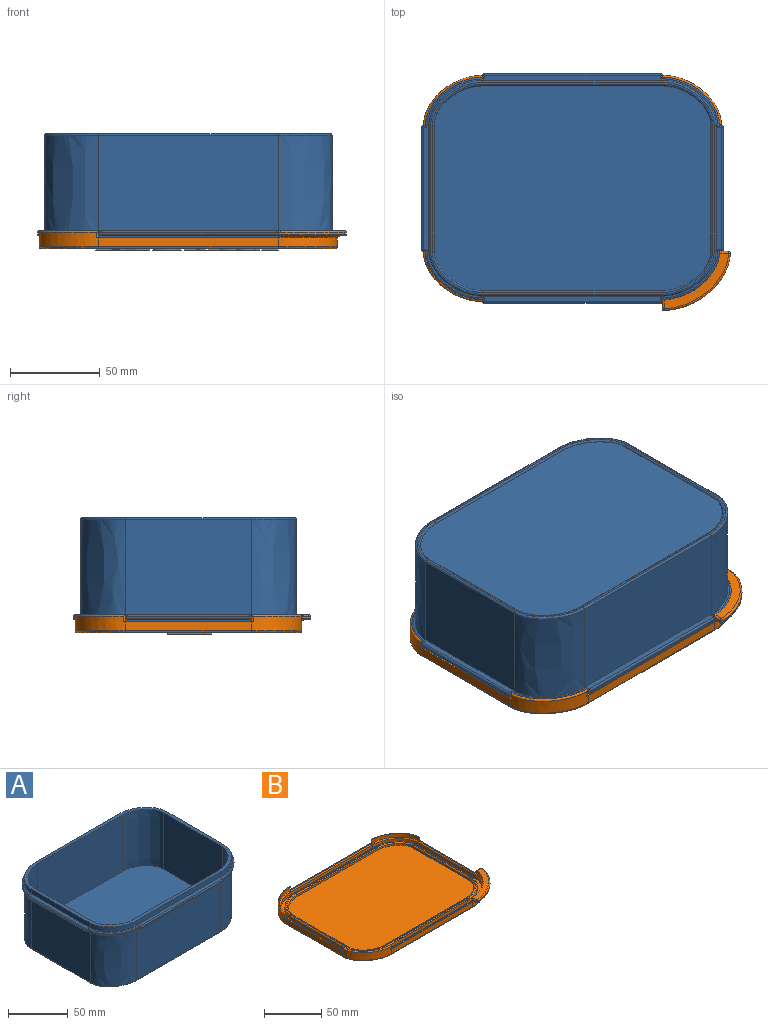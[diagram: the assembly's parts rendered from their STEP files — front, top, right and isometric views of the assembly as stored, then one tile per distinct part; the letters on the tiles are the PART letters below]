
ASSEMBLY  parts=2 mates=1
PART A: 118 faces, bbox 168x128x62 mm
  f0: extruded ~30x25mm, area 213.5mm2, adj f1,f15,f16,f34
  f1: plane 100x5mm, normal (0,-1,0), area 500mm2, adj f0,f2,f16,f34
  f2: extruded ~30x25mm, area 213.5mm2, adj f1,f3,f16,f34
  f3: plane 70x5mm, normal (1,0,0), area 350mm2, adj f2,f4,f16,f34
  f4: extruded ~30x25mm, area 213.5mm2, adj f3,f5,f16,f34
  f5: plane 100x5mm, normal (0,1,0), area 500mm2, adj f4,f6,f16,f34
  f6: extruded ~30x25mm, area 213.5mm2, adj f5,f15,f16,f34
  f7: extruded ~58x27mm, area 2202.8mm2, adj f8,f14,f16,f117
  f8: plane 100x58mm, normal (0,1,0), area 5800mm2, adj f7,f9,f16,f117
  f9: extruded ~58x27mm, area 2202.8mm2, adj f8,f10,f16,f117
  f10: plane 70x58mm, normal (1,0,0), area 4060mm2, adj f9,f11,f16,f117
  f11: extruded ~58x27mm, area 2202.8mm2, adj f10,f12,f16,f117
  f12: plane 100x58mm, normal (0,-1,0), area 5800mm2, adj f11,f13,f16,f117
  f13: extruded ~58x27mm, area 2202.8mm2, adj f12,f14,f16,f117
  f14: plane 70x58mm, normal (-1,0,0), area 4060mm2, adj f7,f13,f16,f117
  f15: plane 70x5mm, normal (-1,0,0), area 350mm2, adj f0,f6,f16,f34
  f16: plane 160x120mm, normal (0,0,1), area 1504mm2, adj f0,f1,f2,f3,f4,f5,f6,f7
  f17: plane 166x126mm, normal (0,0,-1), area 1177.9mm2, adj f67,f68,f70,f71,f74,f75,f77,f78
  f18: plane 1x1mm, normal (0,1,0), area 1mm2, adj f33,f47,f51,f75
  f19: plane 68x1mm, normal (-1,0,0), area 68mm2, adj f45,f51,f53,f71
  f20: plane 1x1mm, normal (0,-1,0), area 1mm2, adj f21,f43,f53,f67
  f21: extruded ~32x27mm, area 45.8mm2, adj f20,f22,f41,f68
  f22: plane 1x1mm, normal (-1,0,0), area 1mm2, adj f21,f39,f55,f70
  f23: plane 98x1mm, normal (0,-1,0), area 98mm2, adj f37,f55,f57,f74
  f24: plane 1x1mm, normal (1,0,0), area 1mm2, adj f25,f35,f57,f78
  f25: extruded ~32x27mm, area 45.8mm2, adj f24,f26,f36,f80
  f26: plane 1x1mm, normal (0,-1,0), area 1mm2, adj f25,f38,f59,f82
  f27: plane 68x1mm, normal (1,0,0), area 68mm2, adj f40,f59,f61,f86
  f28: plane 1x1mm, normal (0,1,0), area 1mm2, adj f29,f42,f61,f90
  f29: extruded ~32x27mm, area 45.8mm2, adj f28,f30,f44,f89
  f30: plane 1x1mm, normal (1,0,0), area 1mm2, adj f29,f46,f63,f87
  f31: plane 98x1mm, normal (0,1,0), area 98mm2, adj f48,f63,f65,f83
  f32: plane 1x1mm, normal (-1,0,0), area 1mm2, adj f33,f50,f65,f79
  f33: extruded ~32x27mm, area 45.8mm2, adj f18,f32,f49,f77
  f34: plane 166x126mm, normal (0,0,1), area 1177.9mm2, adj f0,f1,f2,f3,f4,f5,f6,f15
  f35: cylinder r=1mm len=2mm, axis (0,-1,0), area 2.4mm2, adj f24,f34,f36,f58
  f36: bspline ~33.32x31.21mm, area 72.7mm2, adj f25,f34,f35,f38
  f37: cylinder r=1mm len=98mm, axis (-1,0,0), area 153.9mm2, adj f23,f34,f56,f58
  f38: cylinder r=1mm len=2mm, axis (-1,0,0), area 2.4mm2, adj f26,f34,f36,f60
  f39: cylinder r=1mm len=2mm, axis (0,1,0), area 2.4mm2, adj f22,f34,f41,f56
  f40: cylinder r=1mm len=68mm, axis (0,-1,0), area 106.8mm2, adj f27,f34,f60,f62
  f41: bspline ~33.32x31.21mm, area 72.7mm2, adj f21,f34,f39,f43
  f42: cylinder r=1mm len=2mm, axis (1,0,0), area 2.4mm2, adj f28,f34,f44,f62
  f43: cylinder r=1mm len=2mm, axis (-1,0,0), area 2.4mm2, adj f20,f34,f41,f54
  f44: bspline ~33.32x31.21mm, area 72.7mm2, adj f29,f34,f42,f46
  f45: cylinder r=1mm len=68mm, axis (0,1,0), area 106.8mm2, adj f19,f34,f52,f54
  f46: cylinder r=1mm len=2mm, axis (0,-1,0), area 2.4mm2, adj f30,f34,f44,f64
  f47: cylinder r=1mm len=2mm, axis (1,0,0), area 2.4mm2, adj f18,f34,f49,f52
  f48: cylinder r=1mm len=98mm, axis (1,0,0), area 153.9mm2, adj f31,f34,f64,f66
  f49: bspline ~33.32x31.21mm, area 72.7mm2, adj f33,f34,f47,f50
  f50: cylinder r=1mm len=2mm, axis (0,1,0), area 2.4mm2, adj f32,f34,f49,f66
  f51: cylinder r=1mm len=1mm, axis (0,0,1), area 1.6mm2, adj f18,f19,f52,f73
  f52: sphere r=1mm, area 2.1mm2, adj f45,f47,f51
  f53: cylinder r=1mm len=1mm, axis (0,0,-1), area 1.6mm2, adj f19,f20,f54,f69
  f54: sphere r=1mm, area 1.6mm2, adj f43,f45,f53
  f55: cylinder r=1mm len=1mm, axis (0,0,-1), area 1.6mm2, adj f22,f23,f56,f72
  f56: sphere r=1mm, area 1.6mm2, adj f37,f39,f55
  f57: cylinder r=1mm len=1mm, axis (0,0,1), area 1.6mm2, adj f23,f24,f58,f76
  f58: sphere r=1mm, area 1.6mm2, adj f35,f37,f57
  f59: cylinder r=1mm len=1mm, axis (0,0,-1), area 1.6mm2, adj f26,f27,f60,f84
  f60: sphere r=1mm, area 1.6mm2, adj f38,f40,f59
  f61: cylinder r=1mm len=1mm, axis (0,0,1), area 1.6mm2, adj f27,f28,f62,f88
  f62: sphere r=1mm, area 1mm2, adj f40,f42,f61
  f63: cylinder r=1mm len=1mm, axis (0,0,1), area 1.6mm2, adj f30,f31,f64,f85
  f64: sphere r=1mm, area 1mm2, adj f46,f48,f63
  f65: cylinder r=1mm len=1mm, axis (0,0,-1), area 1.6mm2, adj f31,f32,f66,f81
  f66: sphere r=1mm, area 2.1mm2, adj f48,f50,f65
  f67: cylinder r=1mm len=2mm, axis (1,0,0), area 2.4mm2, adj f17,f20,f68,f69
  f68: bspline ~33.32x31.21mm, area 72.7mm2, adj f17,f21,f67,f70
  f69: sphere r=1mm, area 1.6mm2, adj f53,f67,f71
  f70: cylinder r=1mm len=2mm, axis (0,-1,0), area 2.4mm2, adj f17,f22,f68,f72
  f71: cylinder r=1mm len=68mm, axis (0,-1,0), area 106.8mm2, adj f17,f19,f69,f73
  f72: sphere r=1mm, area 1.6mm2, adj f55,f70,f74
  f73: sphere r=1mm, area 2.1mm2, adj f51,f71,f75
  f74: cylinder r=1mm len=98mm, axis (1,0,0), area 153.9mm2, adj f17,f23,f72,f76
  f75: cylinder r=1mm len=2mm, axis (-1,0,0), area 2.4mm2, adj f17,f18,f73,f77
  f76: sphere r=1mm, area 1.6mm2, adj f57,f74,f78
  f77: bspline ~33.32x31.21mm, area 72.7mm2, adj f17,f33,f75,f79
  f78: cylinder r=1mm len=2mm, axis (0,1,0), area 2.4mm2, adj f17,f24,f76,f80
  f79: cylinder r=1mm len=2mm, axis (0,-1,0), area 2.4mm2, adj f17,f32,f77,f81
  f80: bspline ~33.32x31.21mm, area 72.7mm2, adj f17,f25,f78,f82
  f81: sphere r=1mm, area 2.1mm2, adj f65,f79,f83
  f82: cylinder r=1mm len=2mm, axis (1,0,0), area 2.4mm2, adj f17,f26,f80,f84
  f83: cylinder r=1mm len=98mm, axis (-1,0,0), area 153.9mm2, adj f17,f31,f81,f85
  f84: sphere r=1mm, area 1.6mm2, adj f59,f82,f86
  f85: sphere r=1mm, area 1mm2, adj f63,f83,f87
  f86: cylinder r=1mm len=68mm, axis (0,1,0), area 106.8mm2, adj f17,f27,f84,f88
  f87: cylinder r=1mm len=2mm, axis (0,1,0), area 2.4mm2, adj f17,f30,f85,f89
  f88: sphere r=1mm, area 1mm2, adj f61,f86,f90
  f89: bspline ~33.32x31.21mm, area 72.7mm2, adj f17,f29,f87,f90
  f90: cylinder r=1mm len=2mm, axis (-1,0,0), area 2.4mm2, adj f17,f28,f88,f89
  f91: bspline ~40.83x27.8mm, area 66.2mm2, adj f92,f93,f107,f115
  f92: cylinder r=1mm len=70mm, axis (0,-1,0), area 110mm2, adj f91,f94,f107,f108
  f93: cylinder r=1mm len=100mm, axis (1,0,0), area 157.1mm2, adj f91,f95,f107,f114
  f94: bspline ~40.83x35.83mm, area 66.2mm2, adj f92,f96,f107,f109
  f95: bspline ~40.83x35.83mm, area 66.2mm2, adj f93,f97,f107,f113
  f96: cylinder r=1mm len=100mm, axis (-1,0,0), area 157.1mm2, adj f94,f98,f107,f110
  f97: cylinder r=1mm len=70mm, axis (0,1,0), area 110mm2, adj f95,f98,f107,f112
  f98: bspline ~35.83x32.76mm, area 66.2mm2, adj f96,f97,f107,f111
  f99: cylinder r=1mm len=70mm, axis (0,-1,0), area 110mm2, adj f100,f101,f107,f116
  f100: bspline ~36.6x31.6mm, area 60.6mm2, adj f99,f102,f107,f116
  f101: bspline ~36.6x31.6mm, area 60.6mm2, adj f99,f103,f107,f116
  f102: cylinder r=1mm len=100mm, axis (-1,0,0), area 157.1mm2, adj f100,f104,f107,f116
  f103: cylinder r=1mm len=100mm, axis (1,0,0), area 157.1mm2, adj f101,f105,f107,f116
  f104: bspline ~36.6x31.6mm, area 60.6mm2, adj f102,f106,f107,f116
  f105: bspline ~36.6x31.6mm, area 60.6mm2, adj f103,f106,f107,f116
  f106: cylinder r=1mm len=70mm, axis (0,1,0), area 110mm2, adj f104,f105,f107,f116
  f107: plane 158x118mm, normal (0,0,-1), area 501.2mm2, adj f91,f92,f93,f94,f95,f96,f97,f98
  f108: plane 70x53mm, normal (-1,0,0), area 3710mm2, adj f17,f92,f109,f115
  f109: extruded ~53x30mm, area 2262.6mm2, adj f17,f94,f108,f110
  f110: plane 100x53mm, normal (0,1,0), area 5300mm2, adj f17,f96,f109,f111
  f111: extruded ~53x30mm, area 2262.6mm2, adj f17,f98,f110,f112
  f112: plane 70x53mm, normal (1,0,0), area 3710mm2, adj f17,f97,f111,f113
  f113: extruded ~53x30mm, area 2262.6mm2, adj f17,f95,f112,f114
  f114: plane 100x53mm, normal (0,-1,0), area 5300mm2, adj f17,f93,f113,f115
  f115: extruded ~53x30mm, area 2262.6mm2, adj f17,f91,f108,f114
  f116: plane 154x114mm, normal (0,0,-1), area 16983.5mm2, adj f99,f100,f101,f102,f103,f104,f105,f106
  f117: plane 154x114mm, normal (0,0,1), area 16983.5mm2, adj f7,f8,f9,f10,f11,f12,f13,f14
PART B: 247 faces, bbox 171.4x131.4x11.4 mm
  f0: extruded ~33x28mm, area 237.2mm2, adj f32,f33,f61,f73,f74,f84,f85,f86
  f1: plane 101.04x1mm, normal (0,0,1), area 100.2mm2, adj f32,f38,f51,f73,f104
  f2: plane 102.07x1mm, normal (0,0,1), area 100.4mm2, adj f34,f35,f36,f50,f100,f101
  f3: plane 71.06x1mm, normal (0,0,1), area 70.2mm2, adj f33,f34,f54,f74,f99
  f4: plane 72.11x1mm, normal (0,0,1), area 70.5mm2, adj f36,f37,f38,f47,f102,f103
  f5: extruded ~24x19mm, area 66.5mm2, adj f6,f20,f63,f70
  f6: plane 100x2mm, normal (0,-1,0), area 200mm2, adj f5,f7,f63,f68
  f7: extruded ~24x19mm, area 66.5mm2, adj f6,f8,f63,f66
  f8: plane 70x2mm, normal (-1,0,0), area 140mm2, adj f7,f9,f63,f64
  f9: extruded ~24x19mm, area 66.5mm2, adj f8,f10,f63,f65
  f10: plane 100x2mm, normal (0,1,0), area 200mm2, adj f9,f11,f63,f67
  f11: extruded ~24x19mm, area 66.5mm2, adj f10,f20,f63,f69
  f12: plane 70x3mm, normal (1,0,0), area 210mm2, adj f13,f19,f23,f46
  f13: extruded ~27x22mm, area 113.9mm2, adj f12,f14,f23,f44
  f14: plane 100x3mm, normal (0,1,0), area 300mm2, adj f13,f15,f23,f42
  f15: extruded ~27x22mm, area 113.9mm2, adj f14,f16,f23,f40
  f16: plane 70x3mm, normal (-1,0,0), area 210mm2, adj f15,f17,f23,f39
  f17: extruded ~27x22mm, area 113.9mm2, adj f16,f18,f23,f41
  f18: plane 100x3mm, normal (0,-1,0), area 300mm2, adj f17,f19,f23,f43
  f19: extruded ~27x22mm, area 113.9mm2, adj f12,f18,f23,f45
  f20: plane 70x2mm, normal (1,0,0), area 140mm2, adj f5,f11,f63,f71
  f21: plane 152x112mm, normal (0,0,1), area 482.4mm2, adj f39,f40,f41,f42,f43,f44,f45,f46
  f22: plane 164x124mm, normal (0,0,-1), area 18436.6mm2, adj f55,f56,f57,f58,f59,f60,f61,f62
  f23: plane 162x122mm, normal (0,0,1), area 2017.5mm2, adj f12,f13,f14,f15,f16,f17,f18,f19
  f24: plane 100x3mm, normal (0,1,0), area 300mm2, adj f23,f25,f31,f51
  f25: extruded ~31x26mm, area 132.7mm2, adj f23,f24,f26,f53
  f26: plane 70x3mm, normal (-1,0,0), area 210mm2, adj f23,f25,f27,f54
  f27: extruded ~31x26mm, area 132.7mm2, adj f23,f26,f28,f52
  f28: plane 100x3mm, normal (0,-1,0), area 300mm2, adj f23,f27,f29,f50
  f29: extruded ~31x26mm, area 132.7mm2, adj f23,f28,f30,f48
  f30: plane 70x3mm, normal (1,0,0), area 210mm2, adj f23,f29,f31,f47
  f31: extruded ~31x26mm, area 132.7mm2, adj f23,f24,f30,f49
  f32: plane 100x5mm, normal (0,-1,0), area 500mm2, adj f0,f1,f38,f59
  f33: plane 70x5mm, normal (1,0,0), area 350mm2, adj f0,f3,f34,f62
  f34: extruded ~33x28mm, area 372.8mm2, adj f2,f3,f33,f35,f60,f98,f99,f100
  f35: plane 100x5mm, normal (0,1,0), area 500mm2, adj f2,f34,f36,f58
  f36: extruded ~33x28mm, area 372.8mm2, adj f2,f4,f35,f37,f56,f97,f101,f102
  f37: plane 70x5mm, normal (-1,0,0), area 350mm2, adj f4,f36,f38,f55
  f38: extruded ~33x28mm, area 372.8mm2, adj f1,f4,f32,f37,f57,f96,f103,f104
  f39: cylinder r=1mm len=70mm, axis (0,1,0), area 110mm2, adj f16,f21,f40,f41
  f40: bspline ~35.45x30.45mm, area 58.7mm2, adj f15,f21,f39,f42
  f41: bspline ~35.45x30.45mm, area 58.7mm2, adj f17,f21,f39,f43
  f42: cylinder r=1mm len=100mm, axis (1,0,0), area 157.1mm2, adj f14,f21,f40,f44
  f43: cylinder r=1mm len=100mm, axis (-1,0,0), area 157.1mm2, adj f18,f21,f41,f45
  f44: bspline ~35.45x30.45mm, area 58.7mm2, adj f13,f21,f42,f46
  f45: bspline ~35.45x30.45mm, area 58.7mm2, adj f19,f21,f43,f46
  f46: cylinder r=1mm len=70mm, axis (0,-1,0), area 110mm2, adj f12,f21,f44,f45
  f47: cylinder r=1mm len=70mm, axis (0,-1,0), area 110mm2, adj f4,f30,f48,f49
  f48: bspline ~43.22x38.22mm, area 70.4mm2, adj f29,f47,f50,f77
  f49: bspline ~43.22x38.22mm, area 70.4mm2, adj f31,f47,f51,f78
  f50: cylinder r=1mm len=100mm, axis (-1,0,0), area 157.1mm2, adj f2,f28,f48,f52
  f51: cylinder r=1mm len=100mm, axis (1,0,0), area 157.1mm2, adj f1,f24,f49,f53
  f52: bspline ~43.22x38.22mm, area 70.4mm2, adj f27,f50,f54,f76
  f53: bspline ~43.22x29.81mm, area 70.4mm2, adj f25,f51,f54,f72
  f54: cylinder r=1mm len=70mm, axis (0,1,0), area 110mm2, adj f3,f26,f52,f53
  f55: cylinder r=1mm len=70mm, axis (0,-1,0), area 110mm2, adj f22,f37,f56,f57
  f56: bspline ~45.49x40.49mm, area 73.5mm2, adj f22,f36,f55,f58
  f57: bspline ~45.49x40.49mm, area 73.5mm2, adj f22,f38,f55,f59
  f58: cylinder r=1mm len=100mm, axis (-1,0,0), area 157.1mm2, adj f22,f35,f56,f60
  f59: cylinder r=1mm len=100mm, axis (1,0,0), area 157.1mm2, adj f22,f32,f57,f61
  f60: bspline ~45.49x40.49mm, area 73.5mm2, adj f22,f34,f58,f62
  f61: bspline ~45.49x40.49mm, area 73.5mm2, adj f0,f22,f59,f62
  f62: cylinder r=1mm len=70mm, axis (0,1,0), area 110mm2, adj f22,f33,f60,f61
  f63: plane 148x108mm, normal (0,0,1), area 15533.6mm2, adj f5,f6,f7,f8,f9,f10,f11,f20
  f64: cylinder r=1mm len=70mm, axis (0,1,0), area 110mm2, adj f8,f21,f65,f66
  f65: bspline ~31.42x21.61mm, area 53.1mm2, adj f9,f21,f64,f67
  f66: bspline ~26.61x26.42mm, area 53.1mm2, adj f7,f21,f64,f68
  f67: cylinder r=1mm len=100mm, axis (1,0,0), area 157.1mm2, adj f10,f21,f65,f69
  f68: cylinder r=1mm len=100mm, axis (-1,0,0), area 157.1mm2, adj f6,f21,f66,f70
  f69: bspline ~31.42x26.42mm, area 53.1mm2, adj f11,f21,f67,f71
  f70: bspline ~31.42x26.42mm, area 53.1mm2, adj f5,f21,f68,f71
  f71: cylinder r=1mm len=70mm, axis (0,-1,0), area 110mm2, adj f20,f21,f69,f70
  f72: extruded ~32x27mm, area 182.2mm2, adj f53,f73,f74,f75,f87,f91
  f73: plane 5.36x3.38mm, normal (-1,0,0), area 7.6mm2, adj f0,f1,f72,f83,f86,f87,f94
  f74: plane 5.36x3.38mm, normal (0,1,0), area 7.6mm2, adj f0,f3,f72,f81,f84,f89,f91
  f75: plane 36.08x31.08mm, normal (0,0,1), area 237.5mm2, adj f72,f87,f88,f91
  f76: extruded ~32x27mm, area 183.2mm2, adj f52,f98,f99,f100
  f77: extruded ~32x27mm, area 183.2mm2, adj f48,f97,f101,f102
  f78: extruded ~32x27mm, area 183.2mm2, adj f49,f96,f103,f104
  f79: extruded ~36.95x31.94mm, area 53.2mm2, adj f82,f88,f89,f94
  f80: plane 35.99x31mm, normal (0,0,-1), area 147.9mm2, adj f81,f82,f83,f85
  f81: cylinder r=1mm len=3mm, axis (-1,0,0), area 4.7mm2, adj f74,f80,f84,f90
  f82: bspline ~37.23x32.34mm, area 82.6mm2, adj f79,f80,f90,f93
  f83: cylinder r=1mm len=3mm, axis (0,-1,0), area 4.7mm2, adj f73,f80,f86,f93
  f84: bspline ~2.34x2.23mm, area 2.1mm2, adj f0,f74,f81,f85
  f85: bspline ~33.79x28.79mm, area 72.3mm2, adj f0,f80,f84,f86
  f86: bspline ~2.34x2.25mm, area 2.1mm2, adj f0,f73,f83,f85
  f87: cylinder r=1mm len=5mm, axis (0,1,0), area 7.8mm2, adj f72,f73,f75,f95
  f88: bspline ~37.28x32.48mm, area 82.6mm2, adj f75,f79,f92,f95
  f89: cylinder r=1mm len=1.04mm, axis (0,0,1), area 1.6mm2, adj f74,f79,f90,f92
  f90: sphere r=1mm, area 1mm2, adj f81,f82,f89
  f91: cylinder r=1mm len=5.01mm, axis (1,0,0), area 7.8mm2, adj f72,f74,f75,f92
  f92: sphere r=1mm, area 1mm2, adj f88,f89,f91
  f93: sphere r=1mm, area 1.6mm2, adj f82,f83,f94
  f94: cylinder r=1mm len=1.03mm, axis (0,0,1), area 1.6mm2, adj f73,f79,f93,f95
  f95: sphere r=1mm, area 1.6mm2, adj f87,f88,f94
  f96: bspline ~33x28mm, area 71.9mm2, adj f38,f78,f103,f104
  f97: bspline ~33.34x28.53mm, area 71.9mm2, adj f36,f77,f101,f102
  f98: bspline ~33x28mm, area 71.9mm2, adj f34,f76,f99,f100
  f99: cylinder r=1mm len=4mm, axis (0,0,-1), area 5.6mm2, adj f3,f34,f76,f98
  f100: cylinder r=1mm len=4mm, axis (0,0,-1), area 5.6mm2, adj f2,f34,f76,f98
  f101: cylinder r=1mm len=4mm, axis (0,0,-1), area 5.6mm2, adj f2,f36,f77,f97
  f102: cylinder r=1mm len=4mm, axis (0,0,-1), area 5.6mm2, adj f4,f36,f77,f97
  f103: cylinder r=1mm len=4mm, axis (0,0,-1), area 5.6mm2, adj f4,f38,f78,f96
  f104: cylinder r=1mm len=4mm, axis (0,0,-1), area 5.6mm2, adj f1,f38,f78,f96
  f105: plane 2.77x1mm, normal (1,0,0), area 2.8mm2, adj f22,f106,f128,f129
  f106: plane 8.41x1mm, normal (0,-1,0), area 8.4mm2, adj f22,f105,f107,f129
  f107: plane 2.77x1mm, normal (-1,0,0), area 2.8mm2, adj f22,f106,f108,f129
  f108: plane 2.09x1mm, normal (-0.17,0.99,0), area 2.1mm2, adj f22,f107,f109,f129
  f109: plane 12.54x2.61mm, normal (-0.98,-0.2,0), area 12.8mm2, adj f22,f108,f110,f129
  f110: plane 1x0.1mm, normal (-0.16,-0.99,0), area 0.1mm2, adj f22,f109,f111,f129
  f111: plane 15.69x4.32mm, normal (0.96,-0.27,0), area 16.3mm2, adj f22,f110,f112,f129
  f112: plane 3.38x1mm, normal (0,-1,0), area 3.4mm2, adj f22,f111,f113,f129
  f113: plane 15.69x4.29mm, normal (-0.96,-0.26,0), area 16.3mm2, adj f22,f112,f114,f129
  f114: plane 1x0.1mm, normal (0.16,-0.99,0), area 0.1mm2, adj f22,f113,f115,f129
  f115: plane 12.54x2.63mm, normal (0.98,-0.2,0), area 12.8mm2, adj f22,f114,f116,f129
  f116: plane 2.09x1mm, normal (0.17,0.99,0), area 2.1mm2, adj f22,f115,f117,f129
  f117: plane 2.77x1mm, normal (1,0,0), area 2.8mm2, adj f22,f116,f118,f129
  f118: plane 8.43x1mm, normal (0,-1,0), area 8.4mm2, adj f22,f117,f119,f129
  f119: plane 2.77x1mm, normal (-1,0,0), area 2.8mm2, adj f22,f118,f120,f129
  f120: plane 1.87x1mm, normal (-0.13,0.99,0), area 1.9mm2, adj f22,f119,f121,f129
  f121: plane 19.88x4.67mm, normal (-0.97,0.23,0), area 20.4mm2, adj f22,f120,f122,f129
  f122: plane 4.26x1mm, normal (0,1,0), area 4.3mm2, adj f22,f121,f123,f129
  f123: plane 15.1x4.2mm, normal (0.96,0.27,0), area 15.7mm2, adj f22,f122,f124,f129
  f124: plane 1x0.1mm, normal (0,1,0), area 0.1mm2, adj f22,f123,f125,f129
  f125: plane 15.1x4.2mm, normal (-0.96,0.27,0), area 15.7mm2, adj f22,f124,f126,f129
  f126: plane 4.26x1mm, normal (0,1,0), area 4.3mm2, adj f22,f125,f127,f129
  f127: plane 19.88x4.64mm, normal (0.97,0.23,0), area 20.4mm2, adj f22,f126,f128,f129
  f128: plane 1.89x1mm, normal (0.12,0.99,0), area 1.9mm2, adj f22,f105,f127,f129
  f129: plane 30.07x22.89mm, normal (0,0,-1), area 348.2mm2, adj f105,f106,f107,f108,f109,f110,f111,f112
  f130: plane 5.3x1mm, normal (0,1,0), area 5.3mm2, adj f22,f131,f164,f165
  f131: plane 2.75x1mm, normal (1,0,0), area 2.8mm2, adj f22,f130,f132,f165
  f132: plane 1.4x1mm, normal (0.13,-0.99,0), area 1.4mm2, adj f22,f131,f133,f165
  f133: extruded ~1x0.66mm, area 0.7mm2, adj f22,f132,f134,f165
  f134: extruded ~1x0.74mm, area 0.7mm2, adj f22,f133,f135,f165
  f135: plane 7.02x1mm, normal (1,0,0), area 7mm2, adj f22,f134,f136,f165
  f136: extruded ~4.41x1.97mm, area 5mm2, adj f22,f135,f137,f165
  f137: extruded ~5.13x1.55mm, area 5.5mm2, adj f22,f136,f138,f165
  f138: extruded ~3.54x1mm, area 3.6mm2, adj f22,f137,f139,f165
  f139: extruded ~2.88x1.43mm, area 3.2mm2, adj f22,f138,f140,f165
  f140: plane 3.77x1mm, normal (-1,0,0), area 3.8mm2, adj f22,f139,f141,f165
  f141: plane 3.46x1mm, normal (0,1,0), area 3.5mm2, adj f22,f140,f142,f165
  f142: plane 1.82x1mm, normal (0.99,0.16,0), area 1.8mm2, adj f22,f141,f143,f165
  f143: extruded ~1x0.99mm, area 1.1mm2, adj f22,f142,f144,f165
  f144: extruded ~1.4x1mm, area 1.4mm2, adj f22,f143,f145,f165
  f145: extruded ~2.09x1mm, area 2.3mm2, adj f22,f144,f146,f165
  f146: extruded ~1.9x1mm, area 2.1mm2, adj f22,f145,f147,f165
  f147: plane 1.67x1mm, normal (-1,0,0), area 1.7mm2, adj f22,f146,f148,f165
  f148: plane 2.34x1mm, normal (0,-1,0), area 2.3mm2, adj f22,f147,f149,f165
  f149: extruded ~5.63x1.3mm, area 5.9mm2, adj f22,f148,f150,f165
  f150: extruded ~3.69x1.92mm, area 4.3mm2, adj f22,f149,f151,f165
  f151: extruded ~3.7x1.47mm, area 4.1mm2, adj f22,f150,f152,f165
  f152: extruded ~3.97x1.36mm, area 4.3mm2, adj f22,f151,f153,f165
  f153: extruded ~2.68x1mm, area 2.8mm2, adj f22,f152,f154,f165
  f154: extruded ~1.99x1.52mm, area 2.5mm2, adj f22,f153,f155,f165
  f155: extruded ~1x0.9mm, area 0.9mm2, adj f22,f154,f164,f165
  f156: extruded ~1.54x1mm, area 1.7mm2, adj f157,f163,f165,f166
  f157: extruded ~1.35x1mm, area 1.5mm2, adj f156,f158,f165,f166
  f158: extruded ~1.64x1mm, area 1.9mm2, adj f157,f159,f165,f166
  f159: extruded ~2.21x1mm, area 2.4mm2, adj f158,f160,f165,f166
  f160: plane 2.34x1mm, normal (0,1,0), area 2.3mm2, adj f159,f161,f165,f166
  f161: plane 2.6x1mm, normal (-1,0,0), area 2.6mm2, adj f160,f162,f165,f166
  f162: extruded ~1.32x1.12mm, area 1.8mm2, adj f161,f163,f165,f166
  f163: extruded ~1.89x1mm, area 2mm2, adj f156,f162,f165,f166
  f164: extruded ~1x0.87mm, area 0.9mm2, adj f22,f130,f155,f165
  f165: plane 17.65x15.95mm, normal (0,0,-1), area 178.2mm2, adj f130,f131,f132,f133,f134,f135,f136,f137
  f166: plane 5.31x4.17mm, normal (0,0,-1), area 18.6mm2, adj f156,f157,f158,f159,f160,f161,f162,f163
  f167: plane 2.75x1mm, normal (-1,0,0), area 2.8mm2, adj f22,f168,f185,f186
  f168: plane 8.99x1mm, normal (0,1,0), area 9mm2, adj f22,f167,f169,f186
  f169: plane 2.75x1mm, normal (1,0,0), area 2.8mm2, adj f22,f168,f170,f186
  f170: plane 2.2x1mm, normal (0.21,-0.98,0), area 2.2mm2, adj f22,f169,f171,f186
  f171: plane 8.26x1mm, normal (1,0,0), area 8.3mm2, adj f22,f170,f172,f186
  f172: extruded ~1.12x1mm, area 1.5mm2, adj f22,f171,f173,f186
  f173: extruded ~1.67x1mm, area 1.7mm2, adj f22,f172,f174,f186
  f174: plane 1.89x1mm, normal (-0.02,1,0), area 1.9mm2, adj f22,f173,f175,f186
  f175: plane 4.18x1mm, normal (0.99,0.12,0), area 4.2mm2, adj f22,f174,f176,f186
  f176: extruded ~1x0.67mm, area 0.7mm2, adj f22,f175,f177,f186
  f177: extruded ~1x0.76mm, area 0.8mm2, adj f22,f176,f178,f186
  f178: extruded ~2.18x1mm, area 2.3mm2, adj f22,f177,f179,f186
  f179: extruded ~2.06x1.54mm, area 2.6mm2, adj f22,f178,f180,f186
  f180: plane 2.48x1mm, normal (1,-0.08,0), area 2.5mm2, adj f22,f179,f181,f186
  f181: plane 6.71x1mm, normal (0,-1,0), area 6.7mm2, adj f22,f180,f182,f186
  f182: plane 2.77x1mm, normal (-1,0,0), area 2.8mm2, adj f22,f181,f183,f186
  f183: plane 2.43x1mm, normal (-0.19,0.98,0), area 2.5mm2, adj f22,f182,f184,f186
  f184: plane 10.55x1mm, normal (-1,0,0), area 10.5mm2, adj f22,f183,f185,f186
  f185: plane 2.2x1mm, normal (-0.21,-0.98,0), area 2.2mm2, adj f22,f167,f184,f186
  f186: plane 17.32x12.07mm, normal (0,0,-1), area 117.2mm2, adj f167,f168,f169,f170,f171,f172,f173,f174
  f187: plane 2.45x1mm, normal (-0.19,0.98,0), area 2.5mm2, adj f22,f188,f229,f230
  f188: plane 10.55x1mm, normal (-1,0,0), area 10.5mm2, adj f22,f187,f189,f230
  f189: plane 2.21x1mm, normal (-0.21,-0.98,0), area 2.3mm2, adj f22,f188,f190,f230
  f190: plane 2.75x1mm, normal (-1,0,0), area 2.8mm2, adj f22,f189,f191,f230
  f191: plane 8.77x1mm, normal (0,1,0), area 8.8mm2, adj f22,f190,f192,f230
  f192: plane 2.75x1mm, normal (1,0,0), area 2.8mm2, adj f22,f191,f193,f230
  f193: plane 1.98x1mm, normal (0.23,-0.97,0), area 2mm2, adj f22,f192,f194,f230
  f194: plane 9.18x1mm, normal (1,0,0), area 9.2mm2, adj f22,f193,f195,f230
  f195: extruded ~1.15x1mm, area 1.5mm2, adj f22,f194,f196,f230
  f196: extruded ~1.63x1mm, area 1.7mm2, adj f22,f195,f197,f230
  f197: extruded ~1.89x1mm, area 2.1mm2, adj f22,f196,f198,f230
  f198: extruded ~2.66x1mm, area 2.8mm2, adj f22,f197,f199,f230
  f199: plane 7.09x1mm, normal (-1,0,0), area 7.1mm2, adj f22,f198,f200,f230
  f200: plane 1.86x1mm, normal (-0.25,-0.97,0), area 1.9mm2, adj f22,f199,f201,f230
  f201: plane 2.75x1mm, normal (-1,0,0), area 2.8mm2, adj f22,f200,f202,f230
  f202: plane 8.28x1mm, normal (0,1,0), area 8.3mm2, adj f22,f201,f203,f230
  f203: plane 2.75x1mm, normal (1,0,0), area 2.8mm2, adj f22,f202,f204,f230
  f204: plane 1.86x1mm, normal (0.25,-0.97,0), area 1.9mm2, adj f22,f203,f205,f230
  f205: plane 7.95x1mm, normal (1,0,0), area 8mm2, adj f22,f204,f206,f230
  f206: extruded ~1x0.43mm, area 0.4mm2, adj f22,f205,f207,f230
  f207: extruded ~1x0.51mm, area 0.5mm2, adj f22,f206,f208,f230
  f208: extruded ~1.2x1.14mm, area 1.7mm2, adj f22,f207,f209,f230
  f209: extruded ~1.69x1mm, area 1.8mm2, adj f22,f208,f210,f230
  f210: extruded ~1.87x1mm, area 2.1mm2, adj f22,f209,f211,f230
  f211: extruded ~2.69x1mm, area 2.8mm2, adj f22,f210,f212,f230
  f212: plane 7.09x1mm, normal (-1,0,0), area 7.1mm2, adj f22,f211,f213,f230
  f213: plane 1.98x1mm, normal (-0.23,-0.97,0), area 2mm2, adj f22,f212,f214,f230
  f214: plane 2.75x1mm, normal (-1,0,0), area 2.8mm2, adj f22,f213,f215,f230
  f215: plane 8.79x1mm, normal (0,1,0), area 8.8mm2, adj f22,f214,f216,f230
  f216: plane 2.75x1mm, normal (1,0,0), area 2.8mm2, adj f22,f215,f217,f230
  f217: plane 2.21x1mm, normal (0.21,-0.98,0), area 2.3mm2, adj f22,f216,f218,f230
  f218: plane 7.07x1mm, normal (1,0,0), area 7.1mm2, adj f22,f217,f219,f230
  f219: extruded ~5.29x1.45mm, area 5.6mm2, adj f22,f218,f220,f230
  f220: extruded ~3.97x1.74mm, area 4.5mm2, adj f22,f219,f221,f230
  f221: extruded ~2.96x1mm, area 3.1mm2, adj f22,f220,f222,f230
  f222: extruded ~2.14x2.04mm, area 3mm2, adj f22,f221,f223,f230
  f223: extruded ~2.18x1.76mm, area 2.9mm2, adj f22,f222,f224,f230
  f224: extruded ~2.8x1mm, area 2.9mm2, adj f22,f223,f225,f230
  f225: extruded ~2.85x1mm, area 3mm2, adj f22,f224,f226,f230
  f226: extruded ~2.05x1.9mm, area 2.8mm2, adj f22,f225,f227,f230
  f227: plane 2.25x1mm, normal (1,-0.08,0), area 2.3mm2, adj f22,f226,f228,f230
  f228: plane 6.71x1mm, normal (0,-1,0), area 6.7mm2, adj f22,f227,f229,f230
  f229: plane 2.77x1mm, normal (-1,0,0), area 2.8mm2, adj f22,f187,f228,f230
  f230: plane 29x17.32mm, normal (0,0,-1), area 304.9mm2, adj f187,f188,f189,f190,f191,f192,f193,f194
  f231: plane 2.75x1mm, normal (-1,0,0), area 2.8mm2, adj f22,f232,f240,f241
  f232: plane 9x1mm, normal (0,1,0), area 9mm2, adj f22,f231,f233,f241
  f233: plane 2.75x1mm, normal (1,0,0), area 2.8mm2, adj f22,f232,f234,f241
  f234: plane 2.2x1mm, normal (0.21,-0.98,0), area 2.2mm2, adj f22,f233,f235,f241
  f235: plane 13.78x1mm, normal (1,0,0), area 13.8mm2, adj f22,f234,f236,f241
  f236: plane 7.04x1mm, normal (0,-1,0), area 7mm2, adj f22,f235,f237,f241
  f237: plane 2.77x1mm, normal (-1,0,0), area 2.8mm2, adj f22,f236,f238,f241
  f238: plane 2.45x1mm, normal (-0.19,0.98,0), area 2.5mm2, adj f22,f237,f239,f241
  f239: plane 10.55x1mm, normal (-1,0,0), area 10.5mm2, adj f22,f238,f240,f241
  f240: plane 2.21x1mm, normal (-0.21,-0.98,0), area 2.3mm2, adj f22,f231,f239,f241
  f241: plane 17.01x9.24mm, normal (0,0,-1), area 98.6mm2, adj f231,f232,f233,f234,f235,f236,f237,f238
  f242: plane 3.44x1mm, normal (1,0,0), area 3.4mm2, adj f22,f243,f245,f246
  f243: plane 4.59x1mm, normal (0,-1,0), area 4.6mm2, adj f22,f242,f244,f246
  f244: plane 3.44x1mm, normal (-1,0,0), area 3.4mm2, adj f22,f243,f245,f246
  f245: plane 4.59x1mm, normal (0,1,0), area 4.6mm2, adj f22,f242,f244,f246
  f246: plane 4.59x3.44mm, normal (0,0,-1), area 15.8mm2, adj f242,f243,f244,f245
PLACE A rot(axis=(1,0,0),180deg) t=(-63.72,-134.09,-76.26)mm
PLACE B t=(-63.72,-109.74,-136.26)mm
MATE fastened A.f16 <-> B.f23  axis (0,0,-1) through (-113.72,-138.91,-134.26)mm
